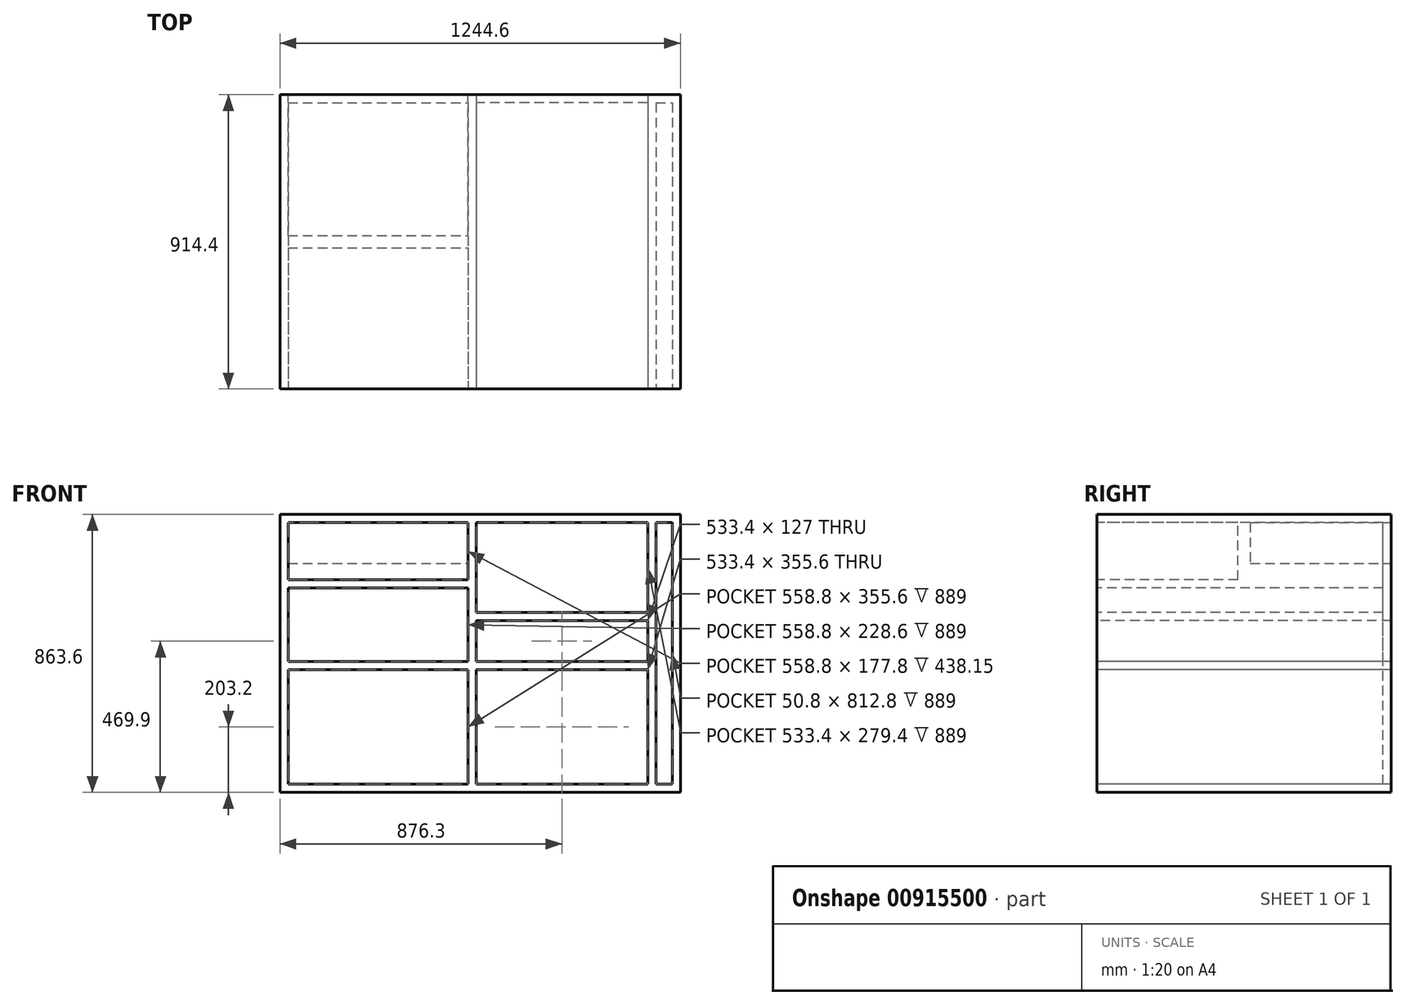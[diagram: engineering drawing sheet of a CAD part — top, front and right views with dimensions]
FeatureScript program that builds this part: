
annotation { "Feature Type Name" : "Feature", "Feature Type Description" : "" }
export const myFeature = defineFeature(function(context is Context, id is Id, definition is map)
    precondition{}
    {
        {
            var Q0;
            Q0=qCreatedBy(makeId("Front.planeOp"),FACE);
            var sketch = newSketch(context, id + "F0", { "sketchPlane" : qUnion([Q0])});
            skLineSegment(sketch, "E0.bottom", {"start": v(622.3, 431.8) * mm, "end": v(-622.3, 431.8) * mm});
            skLineSegment(sketch, "E0.top", {"start": v(622.3, -431.8) * mm, "end": v(-622.3, -431.8) * mm});
            skLineSegment(sketch, "E0.left", {"start": v(622.3, 431.8) * mm, "end": v(622.3, -431.8) * mm});
            skLineSegment(sketch, "E0.right", {"start": v(-622.3, 431.8) * mm, "end": v(-622.3, -431.8) * mm});
            skPoint(sketch, "E0.middle", {"position": v(0, 0) * mm});
            skSolve(sketch);
        }
        {
            var Q0;
            Q0=makeQuery(id+"F0.imprint","IMPRINT",FACE,{"disambiguationData":[TD([[makeQuery(id+"F0.imprint","IMPRINT",EDGE,{"derivedFrom":sQuery(id+"F0.wireOp",EDGE,"E0.bottom")}),1.0]])]});
            extrude(context, id + "F1", {"entities" : qUnion([Q0]), "oppositeDirection" : true, "depth" : 914.4 * mm, "offsetDistance" : 25.4 * mm});
        }
        {
            var Q0;
            Q0=makeQuery(id+"F1.opExtrude","CAP_FACE",FACE,{"disambiguationData":[OSD([sQuery(id+"F0.wireOp",EDGE,"E0.bottom"),sQuery(id+"F0.wireOp",EDGE,"E0.top"),sQuery(id+"F0.wireOp",EDGE,"E0.left"),sQuery(id+"F0.wireOp",EDGE,"E0.right")])],"isStart":true});
            var sketch = newSketch(context, id + "F2", { "sketchPlane" : qUnion([Q0])});
            skLineSegment(sketch, "E1.bottom", {"start": v(-596.9, -406.4) * mm, "end": v(-38.1, -406.4) * mm});
            skLineSegment(sketch, "E1.top", {"start": v(-596.9, -50.8) * mm, "end": v(-38.1, -50.8) * mm});
            skLineSegment(sketch, "E1.left", {"start": v(-596.9, -406.4) * mm, "end": v(-596.9, -50.8) * mm});
            skLineSegment(sketch, "E1.right", {"start": v(-38.1, -406.4) * mm, "end": v(-38.1, -50.8) * mm});
            skSolve(sketch);
        }
        {
            var Q0;
            Q0=makeQuery(id+"F2.imprint","IMPRINT",FACE,{"disambiguationData":[TD([[makeQuery(id+"F2.imprint","IMPRINT",EDGE,{"derivedFrom":sQuery(id+"F2.wireOp",EDGE,"E1.bottom")}),1.0]])]});
            extrude(context, id + "F3", {"entities" : qUnion([Q0]), "operationType" : NewBodyOperationType.REMOVE, "oppositeDirection" : true, "depth" : 889 * mm, "offsetDistance" : 25.4 * mm});
        }
        {
            var Q0;
            Q0=makeQuery(id+"F1.opExtrude","CAP_FACE",FACE,{"disambiguationData":[OSD([sQuery(id+"F0.wireOp",EDGE,"E0.bottom"),sQuery(id+"F0.wireOp",EDGE,"E0.top"),sQuery(id+"F0.wireOp",EDGE,"E0.left"),sQuery(id+"F0.wireOp",EDGE,"E0.right")])],"isStart":true});
            var sketch = newSketch(context, id + "F4", { "sketchPlane" : qUnion([Q0])});
            skLineSegment(sketch, "E2.bottom", {"start": v(-596.9, -25.4) * mm, "end": v(-38.1, -25.4) * mm});
            skLineSegment(sketch, "E2.top", {"start": v(-596.9, 203.2) * mm, "end": v(-38.1, 203.2) * mm});
            skLineSegment(sketch, "E2.left", {"start": v(-596.9, -25.4) * mm, "end": v(-596.9, 203.2) * mm});
            skLineSegment(sketch, "E2.right", {"start": v(-38.1, -25.4) * mm, "end": v(-38.1, 203.2) * mm});
            skSolve(sketch);
        }
        {
            var Q0;
            Q0=makeQuery(id+"F4.imprint","IMPRINT",FACE,{"disambiguationData":[TD([[makeQuery(id+"F4.imprint","IMPRINT",EDGE,{"derivedFrom":sQuery(id+"F4.wireOp",EDGE,"E2.bottom")}),1.0]])]});
            extrude(context, id + "F5", {"entities" : qUnion([Q0]), "operationType" : NewBodyOperationType.REMOVE, "oppositeDirection" : true, "depth" : 889 * mm, "offsetDistance" : 25.4 * mm});
        }
        {
            var Q0;
            Q0=makeQuery(id+"F1.opExtrude","CAP_FACE",FACE,{"disambiguationData":[OSD([sQuery(id+"F0.wireOp",EDGE,"E0.bottom"),sQuery(id+"F0.wireOp",EDGE,"E0.top"),sQuery(id+"F0.wireOp",EDGE,"E0.left"),sQuery(id+"F0.wireOp",EDGE,"E0.right")])],"isStart":true});
            var sketch = newSketch(context, id + "F6", { "sketchPlane" : qUnion([Q0])});
            skLineSegment(sketch, "E3.bottom", {"start": v(-596.9, 228.6) * mm, "end": v(-38.1, 228.6) * mm});
            skLineSegment(sketch, "E3.top", {"start": v(-596.9, 406.4) * mm, "end": v(-38.1, 406.4) * mm});
            skLineSegment(sketch, "E3.left", {"start": v(-596.9, 228.6) * mm, "end": v(-596.9, 406.4) * mm});
            skLineSegment(sketch, "E3.right", {"start": v(-38.1, 228.6) * mm, "end": v(-38.1, 406.4) * mm});
            skSolve(sketch);
        }
        {
            var Q0;
            Q0=makeQuery(id+"F6.imprint","IMPRINT",FACE,{"disambiguationData":[TD([[makeQuery(id+"F6.imprint","IMPRINT",EDGE,{"derivedFrom":sQuery(id+"F6.wireOp",EDGE,"E3.bottom")}),1.0]])]});
            extrude(context, id + "F7", {"entities" : qUnion([Q0]), "operationType" : NewBodyOperationType.REMOVE, "oppositeDirection" : true, "depth" : 438.15 * mm, "offsetDistance" : 25.4 * mm});
        }
        {
            var Q0;
            Q0=makeQuery(id+"F1.opExtrude","CAP_FACE",FACE,{"disambiguationData":[OSD([sQuery(id+"F0.wireOp",EDGE,"E0.bottom"),sQuery(id+"F0.wireOp",EDGE,"E0.top"),sQuery(id+"F0.wireOp",EDGE,"E0.left"),sQuery(id+"F0.wireOp",EDGE,"E0.right")])],"isStart":false});
            var sketch = newSketch(context, id + "F8", { "sketchPlane" : qUnion([Q0])});
            skLineSegment(sketch, "E4.bottom", {"start": v(596.9, 406.4) * mm, "end": v(38.1, 406.4) * mm});
            skLineSegment(sketch, "E4.top", {"start": v(596.9, 279.4) * mm, "end": v(38.1, 279.4) * mm});
            skLineSegment(sketch, "E4.left", {"start": v(596.9, 406.4) * mm, "end": v(596.9, 279.4) * mm});
            skLineSegment(sketch, "E4.right", {"start": v(38.1, 406.4) * mm, "end": v(38.1, 279.4) * mm});
            skSolve(sketch);
        }
        {
            var Q0;
            Q0=makeQuery(id+"F8.imprint","IMPRINT",FACE,{"disambiguationData":[TD([[makeQuery(id+"F8.imprint","IMPRINT",EDGE,{"derivedFrom":sQuery(id+"F8.wireOp",EDGE,"E4.bottom")}),1.0]])]});
            extrude(context, id + "F9", {"entities" : qUnion([Q0]), "operationType" : NewBodyOperationType.REMOVE, "oppositeDirection" : true, "depth" : 438.15 * mm, "offsetDistance" : 25.4 * mm});
        }
        {
            var Q0;
            Q0=makeQuery(id+"F1.opExtrude","CAP_FACE",FACE,{"disambiguationData":[OSD([sQuery(id+"F0.wireOp",EDGE,"E0.bottom"),sQuery(id+"F0.wireOp",EDGE,"E0.top"),sQuery(id+"F0.wireOp",EDGE,"E0.left"),sQuery(id+"F0.wireOp",EDGE,"E0.right")])],"isStart":true});
            var sketch = newSketch(context, id + "F10", { "sketchPlane" : qUnion([Q0])});
            skLineSegment(sketch, "E5.bottom", {"start": v(-12.7, 101.6) * mm, "end": v(520.7, 101.6) * mm});
            skLineSegment(sketch, "E5.top", {"start": v(-12.7, -25.4) * mm, "end": v(520.7, -25.4) * mm});
            skLineSegment(sketch, "E5.left", {"start": v(-12.7, 101.6) * mm, "end": v(-12.7, -25.4) * mm});
            skLineSegment(sketch, "E5.right", {"start": v(520.7, 101.6) * mm, "end": v(520.7, -25.4) * mm});
            skSolve(sketch);
        }
        {
            var Q0;
            Q0=makeQuery(id+"F10.imprint","IMPRINT",FACE,{"disambiguationData":[TD([[makeQuery(id+"F10.imprint","IMPRINT",EDGE,{"derivedFrom":sQuery(id+"F10.wireOp",EDGE,"E5.bottom")}),-1.0]])]});
            extrude(context, id + "F11", {"entities" : qUnion([Q0]), "operationType" : NewBodyOperationType.REMOVE, "oppositeDirection" : true, "depth" : 914.4 * mm, "offsetDistance" : 25.4 * mm});
        }
        {
            var Q0;
            Q0=makeQuery(id+"F1.opExtrude","CAP_FACE",FACE,{"disambiguationData":[OSD([sQuery(id+"F0.wireOp",EDGE,"E0.bottom"),sQuery(id+"F0.wireOp",EDGE,"E0.top"),sQuery(id+"F0.wireOp",EDGE,"E0.left"),sQuery(id+"F0.wireOp",EDGE,"E0.right")])],"isStart":true});
            var sketch = newSketch(context, id + "F12", { "sketchPlane" : qUnion([Q0])});
            skLineSegment(sketch, "E6.bottom", {"start": v(-12.7, -50.8) * mm, "end": v(520.7, -50.8) * mm});
            skLineSegment(sketch, "E6.top", {"start": v(-12.7, -406.4) * mm, "end": v(520.7, -406.4) * mm});
            skLineSegment(sketch, "E6.left", {"start": v(-12.7, -50.8) * mm, "end": v(-12.7, -406.4) * mm});
            skLineSegment(sketch, "E6.right", {"start": v(520.7, -50.8) * mm, "end": v(520.7, -406.4) * mm});
            skSolve(sketch);
        }
        {
            var Q0;
            Q0=makeQuery(id+"F12.imprint","IMPRINT",FACE,{"disambiguationData":[TD([[makeQuery(id+"F12.imprint","IMPRINT",EDGE,{"derivedFrom":sQuery(id+"F12.wireOp",EDGE,"E6.bottom")}),-1.0]])]});
            extrude(context, id + "F13", {"entities" : qUnion([Q0]), "operationType" : NewBodyOperationType.REMOVE, "oppositeDirection" : true, "depth" : 914.4 * mm, "offsetDistance" : 25.4 * mm});
        }
        {
            var Q0;
            Q0=makeQuery(id+"F1.opExtrude","CAP_FACE",FACE,{"disambiguationData":[OSD([sQuery(id+"F0.wireOp",EDGE,"E0.bottom"),sQuery(id+"F0.wireOp",EDGE,"E0.top"),sQuery(id+"F0.wireOp",EDGE,"E0.left"),sQuery(id+"F0.wireOp",EDGE,"E0.right")])],"isStart":true});
            var sketch = newSketch(context, id + "F14", { "sketchPlane" : qUnion([Q0])});
            skLineSegment(sketch, "E7.bottom", {"start": v(546.1, -406.4) * mm, "end": v(596.9, -406.4) * mm});
            skLineSegment(sketch, "E7.top", {"start": v(546.1, 406.4) * mm, "end": v(596.9, 406.4) * mm});
            skLineSegment(sketch, "E7.left", {"start": v(546.1, -406.4) * mm, "end": v(546.1, 406.4) * mm});
            skLineSegment(sketch, "E7.right", {"start": v(596.9, -406.4) * mm, "end": v(596.9, 406.4) * mm});
            skSolve(sketch);
        }
        {
            var Q0;
            Q0=makeQuery(id+"F14.imprint","IMPRINT",FACE,{"disambiguationData":[TD([[makeQuery(id+"F14.imprint","IMPRINT",EDGE,{"derivedFrom":sQuery(id+"F14.wireOp",EDGE,"E7.bottom")}),1.0]])]});
            extrude(context, id + "F15", {"entities" : qUnion([Q0]), "operationType" : NewBodyOperationType.REMOVE, "oppositeDirection" : true, "depth" : 889 * mm, "offsetDistance" : 25.4 * mm});
        }
        {
            var Q0;
            Q0=makeQuery(id+"F1.opExtrude","CAP_FACE",FACE,{"disambiguationData":[OSD([sQuery(id+"F0.wireOp",EDGE,"E0.bottom"),sQuery(id+"F0.wireOp",EDGE,"E0.top"),sQuery(id+"F0.wireOp",EDGE,"E0.left"),sQuery(id+"F0.wireOp",EDGE,"E0.right")])],"isStart":true});
            var sketch = newSketch(context, id + "F16", { "sketchPlane" : qUnion([Q0])});
            skLineSegment(sketch, "E8.bottom", {"start": v(520.7, 127) * mm, "end": v(0, 127) * mm});
            skLineSegment(sketch, "E8.top", {"start": v(520.7, 406.4) * mm, "end": v(0, 406.4) * mm});
            skLineSegment(sketch, "E8.left", {"start": v(520.7, 127) * mm, "end": v(520.7, 406.4) * mm});
            skLineSegment(sketch, "E8.right", {"start": v(0, 127) * mm, "end": v(0, 406.4) * mm});
            skLineSegment(sketch, "E9.bottom", {"start": v(0, 127) * mm, "end": v(-12.7, 127) * mm});
            skLineSegment(sketch, "E9.top", {"start": v(0, 406.4) * mm, "end": v(-12.7, 406.4) * mm});
            skLineSegment(sketch, "E9.right", {"start": v(-12.7, 127) * mm, "end": v(-12.7, 406.4) * mm});
            skSolve(sketch);
        }
        {
            var Q0;
            Q0=makeQuery(id+"F16.imprint","IMPRINT",FACE,{"disambiguationData":[TD([[makeQuery(id+"F16.imprint","IMPRINT",EDGE,{"derivedFrom":sQuery(id+"F16.wireOp",EDGE,"E8.bottom")}),-1.0]])]});
            var Q1;
            Q1=makeQuery(id+"F16.imprint","IMPRINT",FACE,{"disambiguationData":[TD([[makeQuery(id+"F16.imprint","IMPRINT",EDGE,{"derivedFrom":sQuery(id+"F16.wireOp",EDGE,"E9.bottom")}),-1.0]])]});
            extrude(context, id + "F17", {"entities" : qUnion([Q0, Q1]), "operationType" : NewBodyOperationType.REMOVE, "oppositeDirection" : true, "depth" : 889 * mm, "offsetDistance" : 25.4 * mm});
        }
    });
